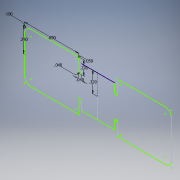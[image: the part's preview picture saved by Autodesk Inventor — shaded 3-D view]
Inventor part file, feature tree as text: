
AUTODESK INVENTOR PART (.ipt)
format: ipt  version: 2017 (Build 210142000, 142)  size: 103,936 bytes
history: native  units: in
note: dims shown in document units (in); Inventor stores cm internally (conversion verified against a paired STEP export)
features: sketch x1
ambient origin geometry x8: Origin, YZ Plane, XZ Plane, XY Plane, X Axis, Y Axis, Z Axis, Center Point
feature tree (1):
  sketch  "Sketch1"  dims[d1=0.39in d2=0.85in d3=0.22in d4=0.04in d5=0.32in d6=0.1in d7=0.05in d8=0.04in]
